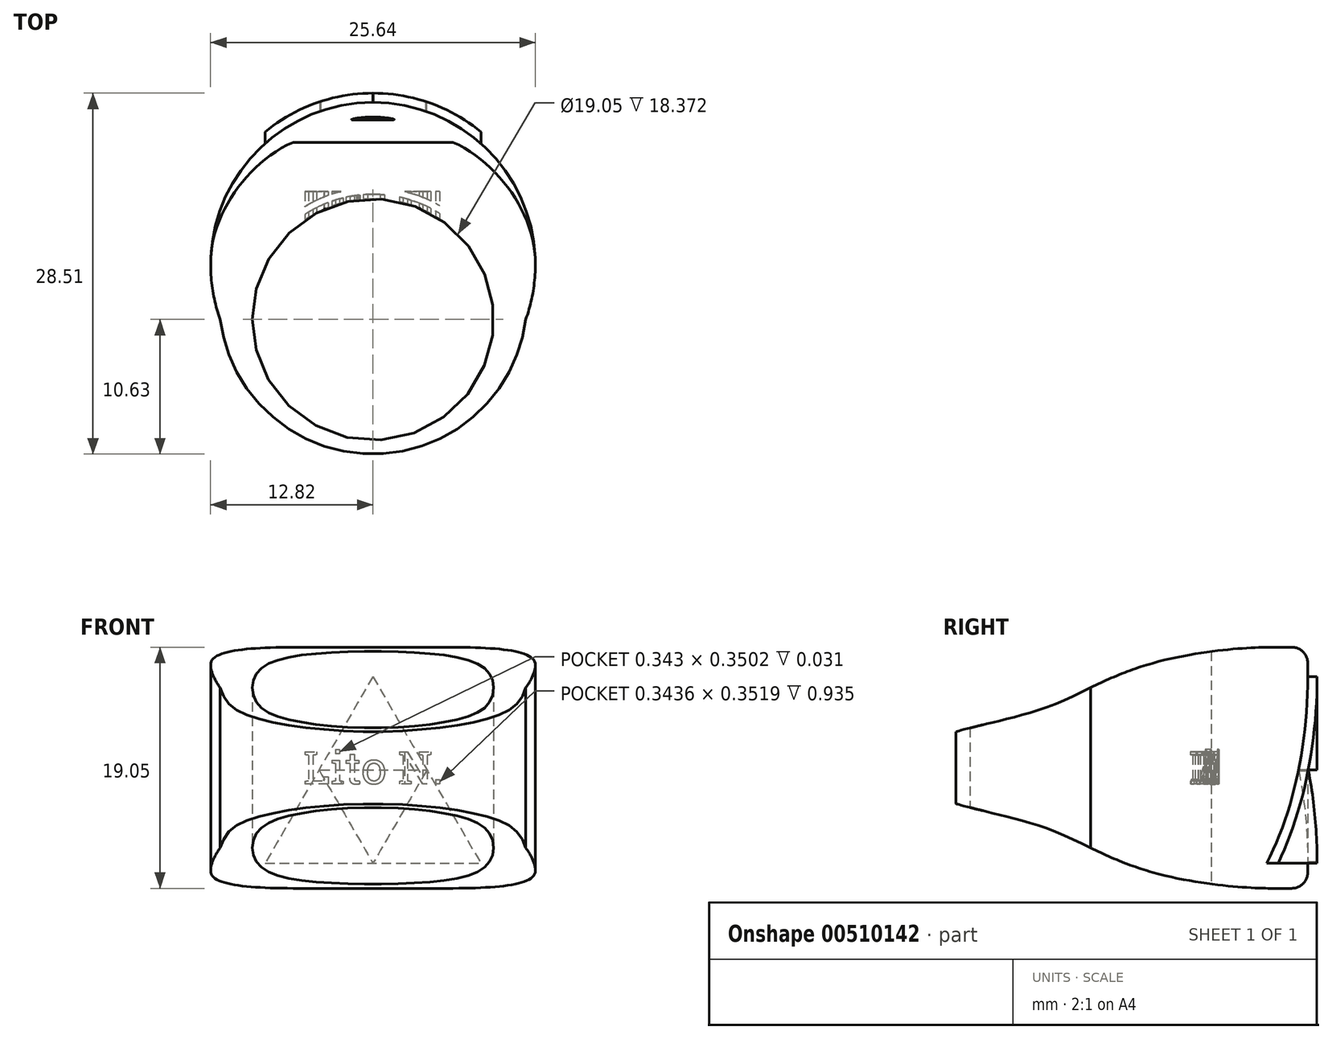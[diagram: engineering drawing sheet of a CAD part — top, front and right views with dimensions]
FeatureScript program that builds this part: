
annotation { "Feature Type Name" : "Feature", "Feature Type Description" : "" }
export const myFeature = defineFeature(function(context is Context, id is Id, definition is map)
    precondition{}
    {
        {
            var Q0;
            Q0=qCreatedBy(makeId("Top.planeOp"),FACE);
            var sketch = newSketch(context, id + "F0", { "sketchPlane" : qUnion([Q0])});
            skCircle(sketch, "E0", {"center": v(0, 0) * mm, "radius": 9.53 * mm});
            skArc(sketch, "E1", {"start": v(-12.06, 0) * mm, "mid": v(0, -10.63) * mm, "end": v(12.07, 0) * mm});
            skArc(sketch, "E2", {"start": v(12.07, 0) * mm, "mid": v(0, 17.14) * mm, "end": v(-12.07, 0) * mm});
            skSolve(sketch);
        }
        {
            var Q0;
            Q0=makeQuery(id+"F0.imprint","IMPRINT",FACE,{"disambiguationData":[TD([[makeQuery(id+"F0.imprint","IMPRINT",EDGE,{"derivedFrom":sQuery(id+"F0.wireOp",EDGE,"E0")}),-1.0]])]});
            extrude(context, id + "F1", {"entities" : qUnion([Q0]), "depth" : 19.05 * mm});
        }
        {
            var Q0;
            Q0=qCreatedBy(makeId("Front.planeOp"),FACE);
            var sketch = newSketch(context, id + "F2", { "sketchPlane" : qUnion([Q0])});
            skText(sketch, "E3", { "text": "Lito N.", "fontName": "RobotoSlab-Regular.ttf"});
            const initialGuessF2  = {"E3": [-0.0055, 0.00824, 1, 0, 0.00257]};
            skSetInitialGuess(sketch, initialGuessF2);
            skSolve(sketch);
        }
        {
            var Q0;
            Q0 = qSketchRegion(id + "F2", true);
            var Q1;
            Q1 = qConstructionFilter(qBodyType(qCreatedBy(id + "F2" ,EDGE), BodyType.WIRE), ConstructionObject.NO);
            extrude(context, id + "F3", {"entities" : qUnion([Q0]), "operationType" : NewBodyOperationType.REMOVE, "surfaceEntities" : qUnion([Q1]), "oppositeDirection" : true, "depth" : 10.1 * mm, "hasSecondDirection" : true, "secondDirectionOppositeDirection" : true, "secondDirectionDepth" : 7.62 * mm});
        }
        {
            var Q0;
            Q0=qCreatedBy(makeId("Top.planeOp"),FACE);
            var sketch = newSketch(context, id + "F4", { "sketchPlane" : qUnion([Q0])});
            skCircle(sketch, "E4", {"center": v(0, 0) * mm, "radius": 9.9 * mm});
            skCircle(sketch, "E5", {"center": v(0, 0) * mm, "radius": 10.42 * mm});
            skSolve(sketch);
        }
        {
            var Q0;
            Q0=makeQuery(id+"F4.imprint","IMPRINT",FACE,{"disambiguationData":[TD([[makeQuery(id+"F4.imprint","IMPRINT",EDGE,{"derivedFrom":sQuery(id+"F4.wireOp",EDGE,"E4")}),-1.0]])]});
            extrude(context, id + "F5", {"entities" : qUnion([Q0]), "operationType" : NewBodyOperationType.ADD, "depth" : 19.05 * mm});
        }
        {
            var Q0;
            Q0=makeQuery(id+"F1.opExtrude","CAP_EDGE",EDGE,{"disambiguationData":[OSD([sQuery(id+"F0.wireOp",EDGE,"E2")])],"isStart":false});
            var Q1;
            Q1=makeQuery(id+"F1.opExtrude","CAP_EDGE",EDGE,{"disambiguationData":[OSD([sQuery(id+"F0.wireOp",EDGE,"E2")])],"isStart":true});
            fillet(context, id + "F6", {"entities" : qUnion([Q0, Q1]), "radius" : 1.27 * mm, "tangentPropagation" : true, "allowEdgeOverflow" : false});
        }
        {
            var Q0;
            Q0=qCreatedBy(makeId("Right.planeOp"),FACE);
            var sketch = newSketch(context, id + "F7", { "sketchPlane" : qUnion([Q0])});
            skLineSegment(sketch, "E6", {"start": v(29.01, 9.53) * mm, "end": v(-18.1, 9.52) * mm});
            skFitSpline(sketch, "E7", {"points": [v(16.27, 19.04) * mm, v(3.6, 17.39) * mm, v(-3.17, 14.41) * mm, v(-10.7, 12.36) * mm], "startDerivative": vector(-34.03, 1.2) * mm, "endDerivative": vector(-25.58, -7.08) * mm});
            skLineSegment(sketch, "E8", {"start": v(16.27, 19.04) * mm, "end": v(19.29, 19.04) * mm});
            skLineSegment(sketch, "E9", {"start": v(19.29, 19.04) * mm, "end": v(19.29, 9.53) * mm});
            skLineSegment(sketch, "E10", {"start": v(-10.7, 12.36) * mm, "end": v(-11.46, 12.36) * mm});
            skLineSegment(sketch, "E11", {"start": v(-11.46, 12.36) * mm, "end": v(-11.46, 9.52) * mm});
            skLineSegment(sketch, "E12", {"start": v(21.42, 9.53) * mm, "end": v(21.42, 22.76) * mm});
            skLineSegment(sketch, "E13", {"start": v(21.42, 22.76) * mm, "end": v(-12.59, 22.76) * mm});
            skLineSegment(sketch, "E14", {"start": v(-12.59, 22.76) * mm, "end": v(-12.59, 9.52) * mm});
            skFitSpline(sketch, "E15.MirrorCS", {"points": [v(16.27, 0.01) * mm, v(3.6, 1.66) * mm, v(-3.17, 4.64) * mm, v(-10.7, 6.7) * mm], "startDerivative": vector(-34.03, -1.2) * mm, "endDerivative": vector(-25.58, 7.08) * mm});
            skLineSegment(sketch, "E16.MirrorCS", {"start": v(16.27, 0.01) * mm, "end": v(19.29, 0.01) * mm});
            skLineSegment(sketch, "E17.MirrorCS", {"start": v(19.29, 0.01) * mm, "end": v(19.29, 9.53) * mm});
            skLineSegment(sketch, "E18.MirrorCS", {"start": v(21.42, -3.71) * mm, "end": v(-12.59, -3.71) * mm});
            skLineSegment(sketch, "E19.MirrorCS", {"start": v(21.42, 9.53) * mm, "end": v(21.42, -3.71) * mm});
            skLineSegment(sketch, "E20.MirrorCS", {"start": v(-12.59, -3.71) * mm, "end": v(-12.59, 9.52) * mm});
            skLineSegment(sketch, "E21.MirrorCS", {"start": v(-11.46, 6.7) * mm, "end": v(-11.46, 9.52) * mm});
            skLineSegment(sketch, "E22.MirrorCS", {"start": v(-10.7, 6.7) * mm, "end": v(-11.46, 6.7) * mm});
            skSolve(sketch);
        }
        {
            var Q0;
            Q0=makeQuery(id+"F7.imprint","IMPRINT",FACE,{"disambiguationData":[TD([[makeQuery(id+"F7.imprint","IMPRINT",EDGE,{"derivedFrom":sQuery(id+"F7.wireOp",EDGE,"E7")}),-1.0]])]});
            var Q1;
            Q1=makeQuery(id+"F7.imprint","IMPRINT",FACE,{"disambiguationData":[TD([[makeQuery(id+"F7.imprint","IMPRINT",EDGE,{"derivedFrom":sQuery(id+"F7.wireOp",EDGE,"E15.MirrorCS")}),1.0]])]});
            extrude(context, id + "F8", {"entities" : qUnion([Q0, Q1]), "operationType" : NewBodyOperationType.REMOVE, "oppositeDirection" : true, "depth" : 25.4 * mm, "hasSecondDirection" : true, "secondDirectionOppositeDirection" : false, "secondDirectionDepth" : 25.4 * mm});
        }
        {
            var Q0;
            Q0=qCreatedBy(makeId("Front.planeOp"),FACE);
            var sketch = newSketch(context, id + "F9", { "sketchPlane" : qUnion([Q0])});
            skLineSegment(sketch, "E23", {"start": v(0, 23.04) * mm, "end": v(0, -13.38) * mm, "construction": true});
            skLineSegment(sketch, "E24", {"start": v(0, 16.73) * mm, "end": v(-8.52, 1.97) * mm});
            skLineSegment(sketch, "E25", {"start": v(-8.52, 1.97) * mm, "end": v(0, 1.97) * mm});
            skLineSegment(sketch, "E26", {"start": v(-4.2, 9.25) * mm, "end": v(-0.06, 2.08) * mm});
            skLineSegment(sketch, "E27", {"start": v(-4.14, 9.35) * mm, "end": v(0, 9.35) * mm});
            skLineSegment(sketch, "E28.MirrorCS", {"start": v(0, 16.73) * mm, "end": v(8.52, 1.97) * mm});
            skLineSegment(sketch, "E29.MirrorCS", {"start": v(4.14, 9.35) * mm, "end": v(0, 9.35) * mm});
            skLineSegment(sketch, "E30.MirrorCS", {"start": v(4.2, 9.25) * mm, "end": v(0.06, 2.08) * mm});
            skLineSegment(sketch, "E31.MirrorCS", {"start": v(8.52, 1.97) * mm, "end": v(0, 1.97) * mm});
            skLineSegment(sketch, "E32", {"start": v(-4.14, 9.35) * mm, "end": v(-4.2, 9.25) * mm});
            skPoint(sketch, "E33.orphan", {"position": v(-4.26, 9.35) * mm});
            skLineSegment(sketch, "E34", {"start": v(0.06, 2.08) * mm, "end": v(-0.06, 2.08) * mm});
            skLineSegment(sketch, "E35", {"start": v(4.14, 9.35) * mm, "end": v(4.2, 9.25) * mm});
            skPoint(sketch, "E36.orphan", {"position": v(4.26, 9.35) * mm});
            skPoint(sketch, "E37.orphan", {"position": v(0, 1.97) * mm});
            skSolve(sketch);
        }
        {
            var Q0;
            Q0=makeQuery(id+"F9.imprint","IMPRINT",FACE,{"disambiguationData":[TD([[makeQuery(id+"F9.imprint","IMPRINT",EDGE,{"derivedFrom":sQuery(id+"F9.wireOp",EDGE,"E24")}),1.0]])]});
            extrude(context, id + "F10", {"entities" : qUnion([Q0]), "operationType" : NewBodyOperationType.ADD, "oppositeDirection" : true, "depth" : 17.88 * mm, "hasSecondDirection" : true, "secondDirectionOppositeDirection" : true, "secondDirectionDepth" : 12.6 * mm});
        }
        {
            var Q0;
            Q0=qCreatedBy(makeId("Top.planeOp"),FACE);
            var sketch = newSketch(context, id + "F11", { "sketchPlane" : qUnion([Q0])});
            skArc(sketch, "E38", {"start": v(12.57, 0) * mm, "mid": v(0, 17.88) * mm, "end": v(-12.57, 0) * mm});
            skLineSegment(sketch, "E39", {"start": v(12.57, 0) * mm, "end": v(15.4, 0) * mm});
            skLineSegment(sketch, "E40", {"start": v(15.4, 0) * mm, "end": v(15.4, 19.65) * mm});
            skLineSegment(sketch, "E41", {"start": v(15.4, 19.65) * mm, "end": v(-16.46, 19.65) * mm});
            skLineSegment(sketch, "E42", {"start": v(-16.46, 19.65) * mm, "end": v(-16.46, 0) * mm});
            skLineSegment(sketch, "E43", {"start": v(-16.46, 0) * mm, "end": v(-12.57, 0) * mm});
            skSolve(sketch);
        }
        {
            var Q0;
            Q0=makeQuery(id+"F11.imprint","IMPRINT",FACE,{"disambiguationData":[TD([[makeQuery(id+"F11.imprint","IMPRINT",EDGE,{"derivedFrom":sQuery(id+"F11.wireOp",EDGE,"E38")}),-1.0]])]});
            extrude(context, id + "F12", {"entities" : qUnion([Q0]), "operationType" : NewBodyOperationType.REMOVE, "depth" : 25.4 * mm});
        }
    });
